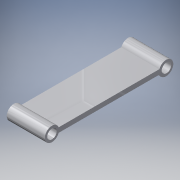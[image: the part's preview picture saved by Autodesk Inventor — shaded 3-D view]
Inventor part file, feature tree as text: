
AUTODESK INVENTOR PART (.ipt)
format: ipt  version: 2016 (Build 200138000, 138)  size: 113,152 bytes
history: native  units: in
note: dims shown in document units (in); Inventor stores cm internally (conversion verified against a paired STEP export)
features: extrude x2, sketch x2
ambient origin geometry x8: Origin, YZ Plane, XZ Plane, XY Plane, X Axis, Y Axis, Z Axis, Center Point
bodies: Solid1 (feature_tree)
feature tree (4):
  extrude  "Extrusion1"  Depth=0.125in
  extrude  "Extrusion2"  Depth=1.0in TaperAngle=0.0deg
  sketch  "Sketch1"  dims[d0=0.125in d2=0.25in]
  sketch  "Sketch2"  dims[d3=0.0625in d4=1.0in d5=0.0in d6=0.0625in d7=0.25in d8=0.0in d9=0.25in d10=1.0in d11=0.0in]
